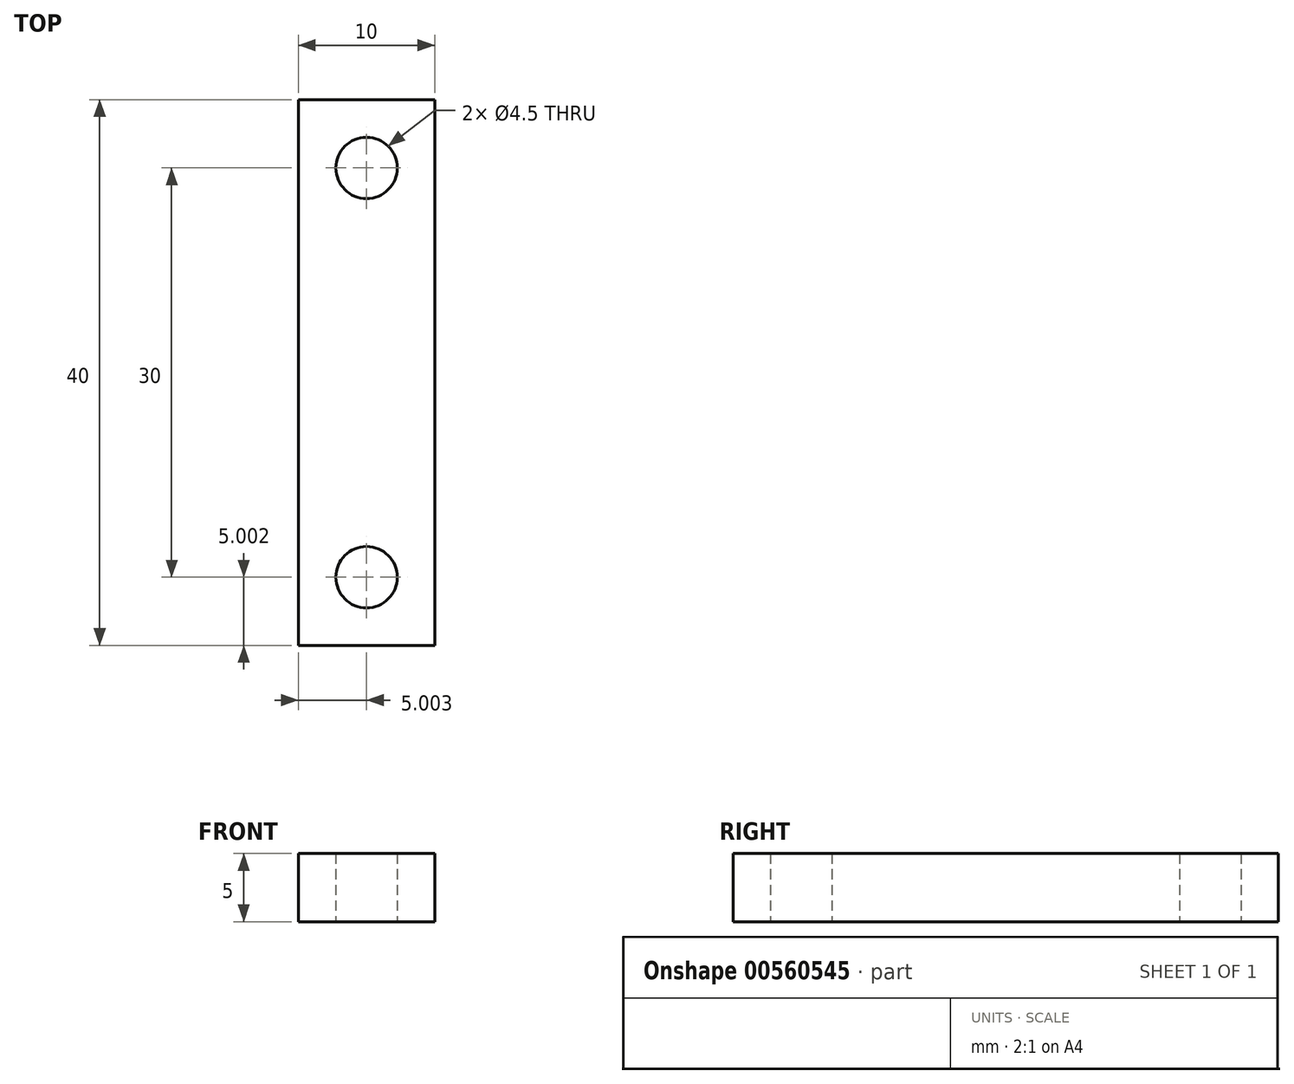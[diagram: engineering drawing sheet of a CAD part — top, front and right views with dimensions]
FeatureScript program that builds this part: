
annotation { "Feature Type Name" : "Feature", "Feature Type Description" : "" }
export const myFeature = defineFeature(function(context is Context, id is Id, definition is map)
    precondition{}
    {
        {
            var Q0;
            Q0=qCreatedBy(makeId("Top.planeOp"),FACE);
            var sketch = newSketch(context, id + "F0", { "sketchPlane" : qUnion([Q0])});
            skLineSegment(sketch, "E0.bottom", {"start": v(-8, 19.72) * mm, "end": v(2, 19.72) * mm});
            skLineSegment(sketch, "E0.top", {"start": v(-8, -20.28) * mm, "end": v(2, -20.28) * mm});
            skLineSegment(sketch, "E0.left", {"start": v(-8, 19.72) * mm, "end": v(-8, -20.28) * mm});
            skLineSegment(sketch, "E0.right", {"start": v(2, 19.72) * mm, "end": v(2, -20.28) * mm});
            skLineSegment(sketch, "E1", {"start": v(-8, -0.28) * mm, "end": v(29.66, -0.28) * mm, "construction": true});
            skLineSegment(sketch, "E2", {"start": v(-3, 31.5) * mm, "end": v(-3, -29.14) * mm, "construction": true});
            skPoint(sketch, "E2.startSnap0", {"position": v(-3, 19.72) * mm});
            skLineSegment(sketch, "E3", {"start": v(7.18, -15.28) * mm, "end": v(-30.8, -15.28) * mm, "construction": true});
            skCircle(sketch, "E4", {"center": v(-3, 14.72) * mm, "radius": 2.25 * mm});
            skCircle(sketch, "E5", {"center": v(-3, -15.28) * mm, "radius": 2.25 * mm});
            skLineSegment(sketch, "E6", {"start": v(8.67, 14.72) * mm, "end": v(-19.55, 14.72) * mm, "construction": true});
            skSolve(sketch);
        }
        {
            var Q0;
            Q0=makeQuery(id+"F0.imprint","IMPRINT",FACE,{"disambiguationData":[TD([[makeQuery(id+"F0.imprint","IMPRINT",EDGE,{"derivedFrom":sQuery(id+"F0.wireOp",EDGE,"E0.bottom")}),-1.0]])]});
            extrude(context, id + "F1", {"entities" : qUnion([Q0]), "depth" : 5 * mm, "offsetDistance" : 25 * mm});
        }
    });
